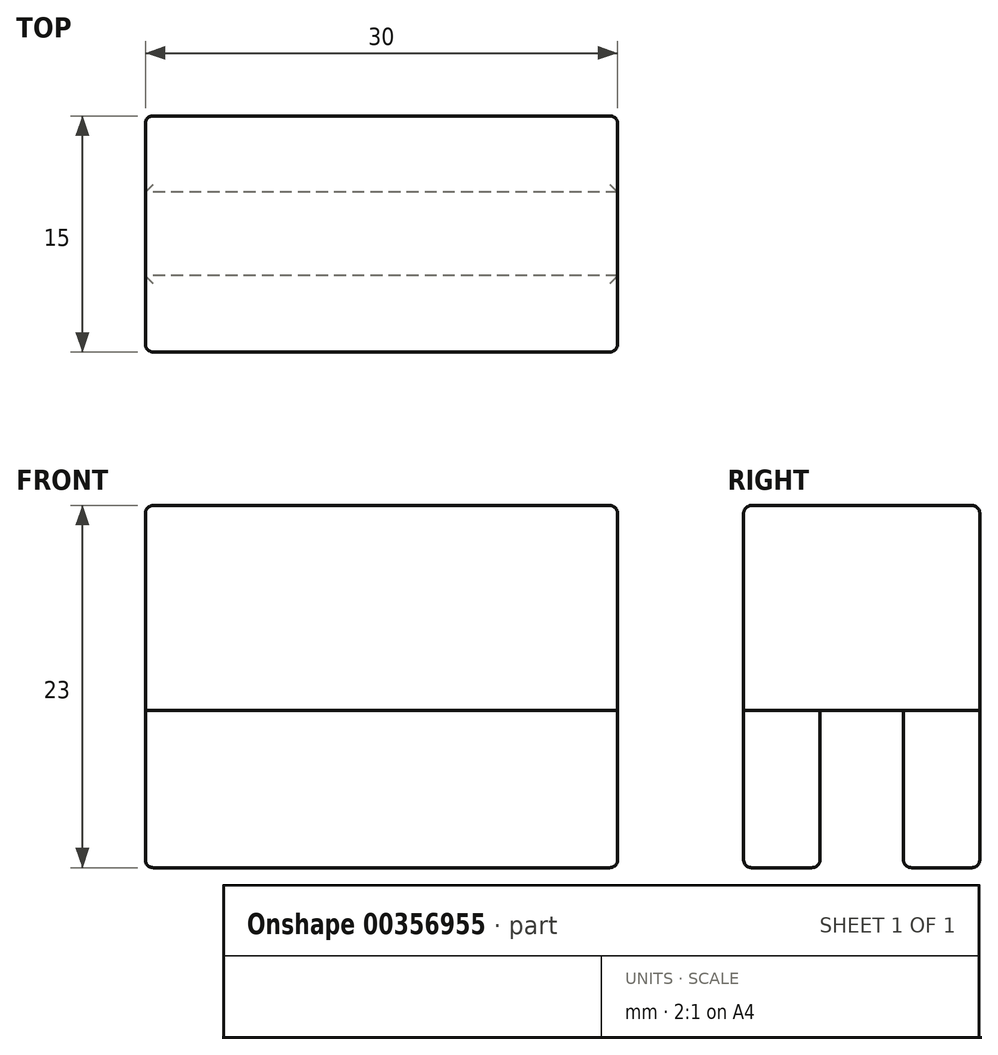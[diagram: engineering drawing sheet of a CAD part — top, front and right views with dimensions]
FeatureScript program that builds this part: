
annotation { "Feature Type Name" : "Feature", "Feature Type Description" : "" }
export const myFeature = defineFeature(function(context is Context, id is Id, definition is map)
    precondition{}
    {
        {
            var Q0;
            Q0=qCreatedBy(makeId("Top.planeOp"),FACE);
            var sketch = newSketch(context, id + "F0", { "sketchPlane" : qUnion([Q0])});
            skLineSegment(sketch, "E0.bottom", {"start": v(0, 0) * mm, "end": v(30, 0) * mm});
            skLineSegment(sketch, "E0.top", {"start": v(0, 15) * mm, "end": v(30, 15) * mm});
            skLineSegment(sketch, "E0.left", {"start": v(0, 0) * mm, "end": v(0, 15) * mm});
            skLineSegment(sketch, "E0.right", {"start": v(30, 0) * mm, "end": v(30, 15) * mm});
            skLineSegment(sketch, "E1.bottom", {"start": v(30, 4.85) * mm, "end": v(0, 4.85) * mm});
            skLineSegment(sketch, "E1.top", {"start": v(30, 10.15) * mm, "end": v(0, 10.15) * mm});
            skLineSegment(sketch, "E1.left", {"start": v(30, 4.85) * mm, "end": v(30, 10.15) * mm});
            skPoint(sketch, "E1.middle", {"position": v(15, 7.5) * mm});
            skLineSegment(sketch, "E2", {"start": v(15, 7.5) * mm, "end": v(30, 7.5) * mm, "construction": true});
            skLineSegment(sketch, "E3", {"start": v(15, 7.5) * mm, "end": v(15, 15) * mm, "construction": true});
            skPoint(sketch, "E3.endSnap0", {"position": v(15, 15) * mm});
            skSolve(sketch);
        }
        {
            var Q0;
            {var subQ0=sQuery(id+"F0.wireOp",EDGE,"E0.top");Q0=makeQuery(id+"F0.imprint","IMPRINT",FACE,{"disambiguationData":[TD([[makeQuery(id+"F0.imprint","IMPRINT",EDGE,{"derivedFrom":subQ0}),-1.0]])]});}
            var Q1;
            {var subQ0=sQuery(id+"F0.wireOp",EDGE,"E0.bottom");Q1=makeQuery(id+"F0.imprint","IMPRINT",FACE,{"disambiguationData":[TD([[makeQuery(id+"F0.imprint","IMPRINT",EDGE,{"derivedFrom":subQ0}),1.0]])]});}
            extrude(context, id + "F1", {"entities" : qUnion([Q0, Q1]), "depth" : 10 * mm});
        }
        {
            var Q0;
            Q0=makeQuery(id+"F1.opExtrude","CAP_FACE",FACE,{"disambiguationData":[OSD([sQuery(id+"F0.wireOp",EDGE,"E0.top"),sQuery(id+"F0.wireOp",EDGE,"E0.left"),sQuery(id+"F0.wireOp",EDGE,"E0.right"),sQuery(id+"F0.wireOp",EDGE,"E1.top")])],"isStart":false});
            var sketch = newSketch(context, id + "F2", { "sketchPlane" : qUnion([Q0])});
            skLineSegment(sketch, "E4.bottom", {"start": v(0, 0) * mm, "end": v(30, 0) * mm});
            skLineSegment(sketch, "E4.top", {"start": v(0, 15) * mm, "end": v(30, 15) * mm});
            skLineSegment(sketch, "E4.left", {"start": v(0, 0) * mm, "end": v(0, 15) * mm});
            skLineSegment(sketch, "E4.right", {"start": v(30, 0) * mm, "end": v(30, 15) * mm});
            skSolve(sketch);
        }
        {
            var Q0;
            {var subQ0=sQuery(id+"F2.wireOp",EDGE,"E4.top");Q0=makeQuery(id+"F2.imprint","IMPRINT",FACE,{"disambiguationData":[TD([[makeQuery(id+"F2.imprint","IMPRINT",EDGE,{"derivedFrom":subQ0}),-1.0]])]});}
            var Q1;
            {var subQ0=sQuery(id+"F2.wireOp",EDGE,"E4.bottom");Q1=makeQuery(id+"F2.imprint","IMPRINT",FACE,{"disambiguationData":[TD([[makeQuery(id+"F2.imprint","IMPRINT",EDGE,{"derivedFrom":subQ0}),1.0]])]});}
            extrude(context, id + "F3", {"entities" : qUnion([Q0, Q1]), "depth" : 13 * mm});
        }
        {
            var Q0;
            Q0=makeQuery(id+"F3.opExtrude","CAP_EDGE",EDGE,{"disambiguationData":[OSD([sQuery(id+"F2.wireOp",EDGE,"E4.top")])],"isStart":false});
            var Q1;
            Q1=makeQuery(id+"F3.opExtrude","CAP_FACE",FACE,{"disambiguationData":[OSD([sQuery(id+"F2.wireOp",EDGE,"E4.bottom"),sQuery(id+"F2.wireOp",EDGE,"E4.top"),sQuery(id+"F2.wireOp",EDGE,"E4.left"),sQuery(id+"F2.wireOp",EDGE,"E4.right")])],"isStart":false});
            var Q2;
            Q2=makeQuery(id+"F3.opExtrude","SWEPT_EDGE",EDGE,{"disambiguationData":[OSD([sQuery(id+"F2.wireOp",EDGE,"E4.top"),sQuery(id+"F2.wireOp",EDGE,"E4.left")])]});
            var Q3;
            Q3=makeQuery(id+"F1.opExtrude","SWEPT_EDGE",EDGE,{"disambiguationData":[OSD([sQuery(id+"F0.wireOp",EDGE,"E0.top"),sQuery(id+"F0.wireOp",EDGE,"E0.left")])]});
            var Q4;
            Q4=makeQuery(id+"F1.opExtrude","SWEPT_EDGE",EDGE,{"disambiguationData":[OSD([sQuery(id+"F0.wireOp",EDGE,"E0.top"),sQuery(id+"F0.wireOp",EDGE,"E0.right")])]});
            var Q5;
            Q5=makeQuery(id+"F3.opExtrude","SWEPT_EDGE",EDGE,{"disambiguationData":[OSD([sQuery(id+"F2.wireOp",EDGE,"E4.top"),sQuery(id+"F2.wireOp",EDGE,"E4.right")])]});
            var Q6;
            Q6=makeQuery(id+"F1.opExtrude","SWEPT_EDGE",EDGE,{"disambiguationData":[OSD([sQuery(id+"F0.wireOp",EDGE,"E0.bottom"),sQuery(id+"F0.wireOp",EDGE,"E0.right")])]});
            var Q7;
            Q7=makeQuery(id+"F3.opExtrude","SWEPT_EDGE",EDGE,{"disambiguationData":[OSD([sQuery(id+"F2.wireOp",EDGE,"E4.bottom"),sQuery(id+"F2.wireOp",EDGE,"E4.right")])]});
            var Q8;
            Q8=makeQuery(id+"F3.opExtrude","SWEPT_EDGE",EDGE,{"disambiguationData":[OSD([sQuery(id+"F2.wireOp",EDGE,"E4.bottom"),sQuery(id+"F2.wireOp",EDGE,"E4.left")])]});
            var Q9;
            Q9=makeQuery(id+"F1.opExtrude","SWEPT_EDGE",EDGE,{"disambiguationData":[OSD([sQuery(id+"F0.wireOp",EDGE,"E0.bottom"),sQuery(id+"F0.wireOp",EDGE,"E0.left")])]});
            var Q10;
            {var subQ0=sQuery(id+"F0.wireOp",EDGE,"E0.left");Q10=makeQuery(id+"F1.opExtrude","CAP_EDGE",EDGE,{"disambiguationData":[OSD([subQ0]),TDD([makeQuery(id+"F0.imprint","IMPRINT",EDGE,{"disambiguationData":[TD([[makeQuery(id+"F0.imprint","INTERSECT",VERTEX,{"derivedFrom":[sQuery(id+"F0.wireOp",EDGE,"E0.bottom"),subQ0]}),-1.0]])],"derivedFrom":subQ0})])],"isStart":true});}
            var Q11;
            Q11=makeQuery(id+"F1.opExtrude","CAP_EDGE",EDGE,{"disambiguationData":[OSD([sQuery(id+"F0.wireOp",EDGE,"E0.bottom")])],"isStart":true});
            var Q12;
            {var subQ0=sQuery(id+"F0.wireOp",EDGE,"E0.right");Q12=makeQuery(id+"F1.opExtrude","CAP_EDGE",EDGE,{"disambiguationData":[OSD([subQ0]),TDD([makeQuery(id+"F0.imprint","IMPRINT",EDGE,{"disambiguationData":[TD([[makeQuery(id+"F0.imprint","INTERSECT",VERTEX,{"derivedFrom":[sQuery(id+"F0.wireOp",EDGE,"E0.bottom"),subQ0]}),-1.0]])],"derivedFrom":subQ0})])],"isStart":true});}
            var Q13;
            Q13=makeQuery(id+"F1.opExtrude","CAP_EDGE",EDGE,{"disambiguationData":[OSD([sQuery(id+"F0.wireOp",EDGE,"E1.bottom")])],"isStart":true});
            var Q14;
            {var subQ0=sQuery(id+"F0.wireOp",EDGE,"E0.left");Q14=makeQuery(id+"F1.opExtrude","CAP_EDGE",EDGE,{"disambiguationData":[OSD([subQ0]),TDD([makeQuery(id+"F0.imprint","IMPRINT",EDGE,{"disambiguationData":[TD([[makeQuery(id+"F0.imprint","INTERSECT",VERTEX,{"derivedFrom":[sQuery(id+"F0.wireOp",EDGE,"E0.top"),subQ0]}),1.0]])],"derivedFrom":subQ0})])],"isStart":true});}
            var Q15;
            {var subQ0=sQuery(id+"F0.wireOp",EDGE,"E0.right");Q15=makeQuery(id+"F1.opExtrude","CAP_EDGE",EDGE,{"disambiguationData":[OSD([subQ0]),TDD([makeQuery(id+"F0.imprint","IMPRINT",EDGE,{"disambiguationData":[TD([[makeQuery(id+"F0.imprint","INTERSECT",VERTEX,{"derivedFrom":[sQuery(id+"F0.wireOp",EDGE,"E0.top"),subQ0]}),1.0]])],"derivedFrom":subQ0})])],"isStart":true});}
            var Q16;
            Q16=makeQuery(id+"F1.opExtrude","CAP_EDGE",EDGE,{"disambiguationData":[OSD([sQuery(id+"F0.wireOp",EDGE,"E1.top")])],"isStart":true});
            var Q17;
            Q17=makeQuery(id+"F1.opExtrude","CAP_EDGE",EDGE,{"disambiguationData":[OSD([sQuery(id+"F0.wireOp",EDGE,"E0.top")])],"isStart":true});
            fillet(context, id + "F4", {"entities" : qUnion([Q0, Q1, Q2, Q3, Q4, Q5, Q6, Q7, Q8, Q9, Q10, Q11, Q12, Q13, Q14, Q15, Q16, Q17]), "radius" : 0.5 * mm, "tangentPropagation" : true, "allowEdgeOverflow" : false});
        }
    });
